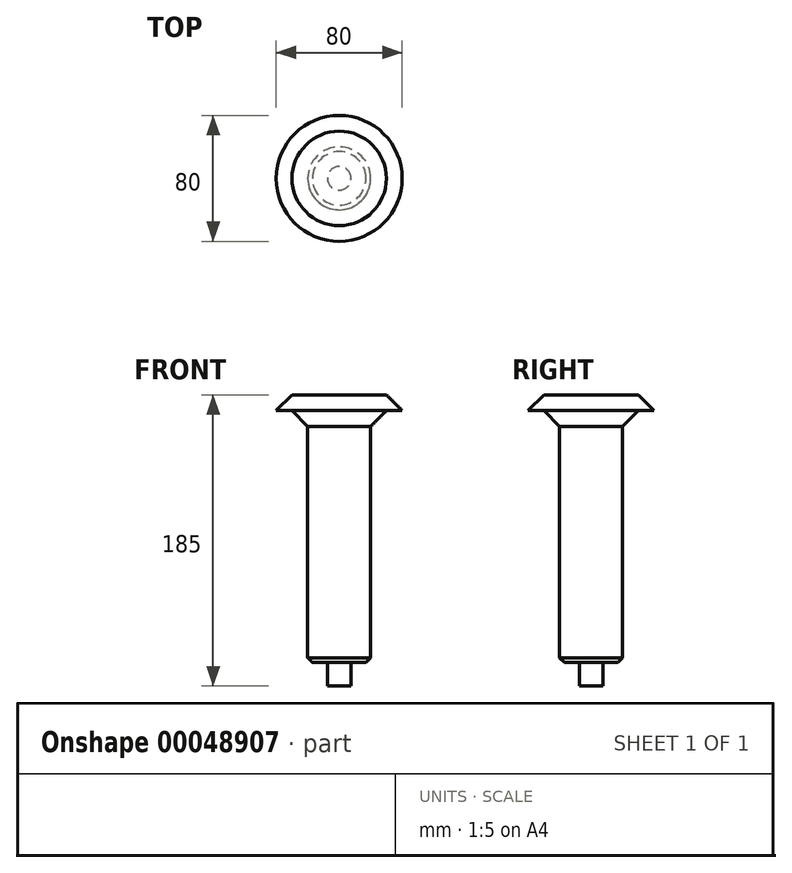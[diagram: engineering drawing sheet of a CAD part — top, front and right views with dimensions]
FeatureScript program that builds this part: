
annotation { "Feature Type Name" : "Feature", "Feature Type Description" : "" }
export const myFeature = defineFeature(function(context is Context, id is Id, definition is map)
    precondition{}
    {
        {
            var Q0;
            Q0=qCreatedBy(makeId("Top.planeOp"),FACE);
            var sketch = newSketch(context, id + "F0", { "sketchPlane" : qUnion([Q0])});
            skCircle(sketch, "E0", {"center": v(0, 0) * mm, "radius": 40 * mm});
            skSolve(sketch);
        }
        {
            var Q0;
            Q0 = qSketchRegion(id + "F0", true);
            extrude(context, id + "F1", {"entities" : qUnion([Q0]), "depth" : 10 * mm});
        }
        {
            var Q0;
            Q0=qCreatedBy(makeId("Top.planeOp"),FACE);
            var sketch = newSketch(context, id + "F2", { "sketchPlane" : qUnion([Q0])});
            skCircle(sketch, "E1", {"center": v(0, 0) * mm, "radius": 30 * mm});
            skSolve(sketch);
        }
        {
            var Q0;
            Q0=makeQuery(id+"F2.imprint","IMPRINT",FACE,{"disambiguationData":[TD([[makeQuery(id+"F2.imprint","IMPRINT",EDGE,{"derivedFrom":sQuery(id+"F2.wireOp",EDGE,"E1")}),1.0]])]});
            extrude(context, id + "F3", {"entities" : qUnion([Q0]), "operationType" : NewBodyOperationType.ADD, "oppositeDirection" : true, "depth" : 10 * mm});
        }
        {
            var Q0;
            Q0=makeQuery(id+"F3.opExtrude","CAP_FACE",FACE,{"disambiguationData":[OSD([sQuery(id+"F2.wireOp",EDGE,"E1")])],"isStart":false});
            var sketch = newSketch(context, id + "F4", { "sketchPlane" : qUnion([Q0])});
            skCircle(sketch, "E2", {"center": v(0, 0) * mm, "radius": 20 * mm});
            skSolve(sketch);
        }
        {
            var Q0;
            Q0=makeQuery(id+"F4.imprint","IMPRINT",FACE,{"disambiguationData":[TD([[makeQuery(id+"F4.imprint","IMPRINT",EDGE,{"derivedFrom":sQuery(id+"F4.wireOp",EDGE,"E2")}),1.0]])]});
            extrude(context, id + "F5", {"entities" : qUnion([Q0]), "operationType" : NewBodyOperationType.ADD, "depth" : 150 * mm});
        }
        {
            var Q0;
            Q0=makeQuery(id+"F5.opExtrude","CAP_FACE",FACE,{"disambiguationData":[OSD([sQuery(id+"F4.wireOp",EDGE,"E2")])],"isStart":false});
            var sketch = newSketch(context, id + "F6", { "sketchPlane" : qUnion([Q0])});
            skCircle(sketch, "E3", {"center": v(0, 0) * mm, "radius": 7.5 * mm});
            skSolve(sketch);
        }
        {
            var Q0;
            Q0=makeQuery(id+"F6.imprint","IMPRINT",FACE,{"disambiguationData":[TD([[makeQuery(id+"F6.imprint","IMPRINT",EDGE,{"derivedFrom":sQuery(id+"F6.wireOp",EDGE,"E3")}),1.0]])]});
            extrude(context, id + "F7", {"entities" : qUnion([Q0]), "operationType" : NewBodyOperationType.ADD, "depth" : 15 * mm});
        }
        {
            var Q0;
            Q0=makeQuery(id+"F1.opExtrude","CAP_EDGE",EDGE,{"disambiguationData":[OSD([sQuery(id+"F0.wireOp",EDGE,"E0")])],"isStart":false});
            chamfer(context, id + "F8", {"entities" : qUnion([Q0]), "chamferType" : ChamferType.OFFSET_ANGLE, "width" : 10 * mm, "oppositeDirection" : false, "angle" : 45 * degree, "tangentPropagation" : true});
        }
        {
            var Q0;
            Q0=makeQuery(id+"F3.opExtrude","CAP_EDGE",EDGE,{"disambiguationData":[OSD([sQuery(id+"F2.wireOp",EDGE,"E1")])],"isStart":false});
            chamfer(context, id + "F9", {"entities" : qUnion([Q0]), "width" : 10 * mm, "tangentPropagation" : true});
        }
        {
            var Q0;
            Q0=makeQuery(id+"F5.opExtrude","CAP_EDGE",EDGE,{"disambiguationData":[OSD([sQuery(id+"F4.wireOp",EDGE,"E2")])],"isStart":false});
            chamfer(context, id + "F10", {"entities" : qUnion([Q0]), "width" : 3 * mm, "tangentPropagation" : true});
        }
    });
